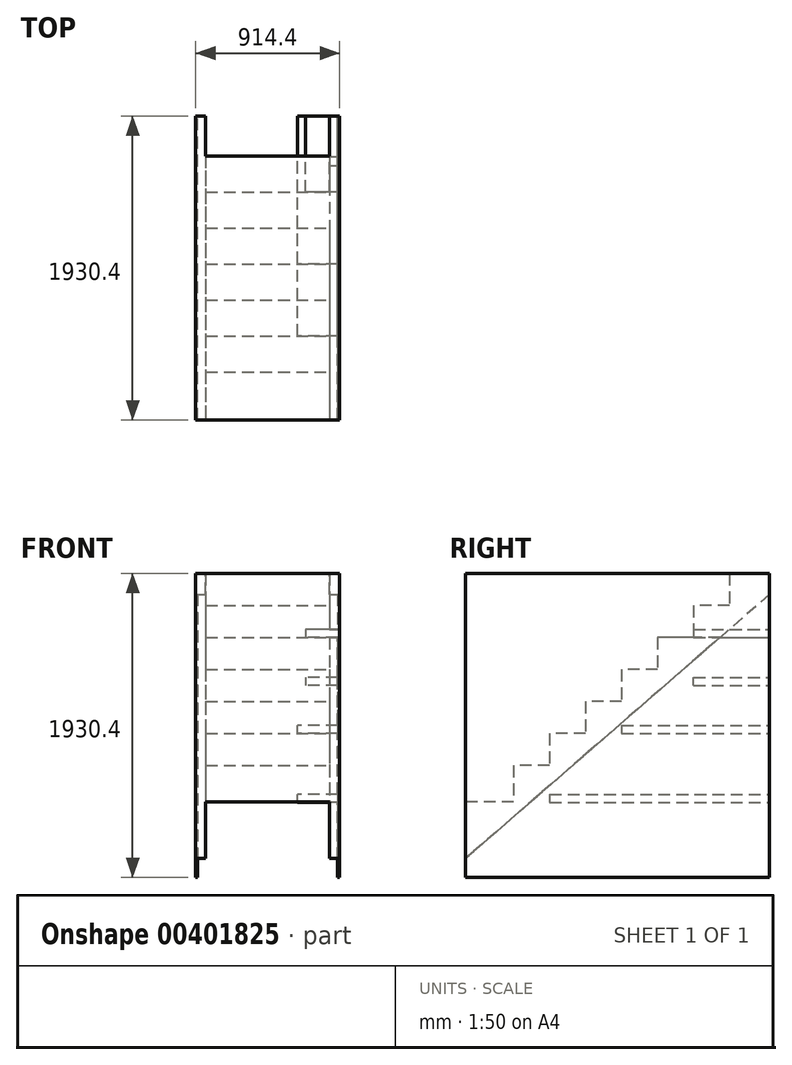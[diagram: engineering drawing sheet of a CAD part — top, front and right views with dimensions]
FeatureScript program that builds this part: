
annotation { "Feature Type Name" : "Feature", "Feature Type Description" : "" }
export const myFeature = defineFeature(function(context is Context, id is Id, definition is map)
    precondition{}
    {
        {
            var Q0;
            Q0=qCreatedBy(makeId("Front.planeOp"),FACE);
            var sketch = newSketch(context, id + "F0", { "sketchPlane" : qUnion([Q0])});
            skLineSegment(sketch, "E0.bottom", {"start": v(-457.2, 965.2) * mm, "end": v(457.2, 965.2) * mm});
            skLineSegment(sketch, "E0.top", {"start": v(-457.2, -965.2) * mm, "end": v(457.2, -965.2) * mm});
            skLineSegment(sketch, "E0.left", {"start": v(-457.2, 965.2) * mm, "end": v(-457.2, -965.2) * mm});
            skLineSegment(sketch, "E0.right", {"start": v(457.2, 965.2) * mm, "end": v(457.2, -965.2) * mm});
            skPoint(sketch, "E0.middle", {"position": v(0, 0) * mm});
            skSolve(sketch);
        }
        {
            var Q0;
            Q0 = qSketchRegion(id + "F0", true);
            extrude(context, id + "F1", {"entities" : qUnion([Q0]), "depth" : 1930.4 * mm});
        }
        {
            var Q0;
            Q0=qCreatedBy(makeId("Right.planeOp"),FACE);
            var sketch = newSketch(context, id + "F2", { "sketchPlane" : qUnion([Q0])});
            skLineSegment(sketch, "E1", {"start": v(-254, 965.2) * mm, "end": v(-254, 762) * mm});
            skLineSegment(sketch, "E2", {"start": v(-254, 762) * mm, "end": v(-482.6, 762) * mm});
            skLineSegment(sketch, "E3", {"start": v(-482.6, 762) * mm, "end": v(-482.6, 558.8) * mm});
            skLineSegment(sketch, "E4", {"start": v(-482.6, 558.8) * mm, "end": v(-711.2, 558.8) * mm});
            skLineSegment(sketch, "E5", {"start": v(-711.2, 558.8) * mm, "end": v(-711.2, 355.6) * mm});
            skLineSegment(sketch, "E6", {"start": v(-711.2, 355.6) * mm, "end": v(-939.8, 355.6) * mm});
            skLineSegment(sketch, "E7", {"start": v(-939.8, 355.6) * mm, "end": v(-939.8, 152.4) * mm});
            skLineSegment(sketch, "E8", {"start": v(-939.8, 152.4) * mm, "end": v(-1168.4, 152.4) * mm});
            skLineSegment(sketch, "E9", {"start": v(-1168.4, 152.4) * mm, "end": v(-1168.4, -50.8) * mm});
            skLineSegment(sketch, "E10", {"start": v(-1168.4, -50.8) * mm, "end": v(-1397, -50.8) * mm});
            skLineSegment(sketch, "E11", {"start": v(-1397, -50.8) * mm, "end": v(-1397, -254) * mm});
            skLineSegment(sketch, "E12", {"start": v(-1397, -254) * mm, "end": v(-1625.6, -254) * mm});
            skLineSegment(sketch, "E13", {"start": v(-1625.6, -254) * mm, "end": v(-1625.6, -485.14) * mm});
            skLineSegment(sketch, "E14", {"start": v(-1625.6, -485.14) * mm, "end": v(-1930.4, -485.14) * mm});
            skLineSegment(sketch, "E15", {"start": v(-1930.4, -485.14) * mm, "end": v(-1930.4, -969.01) * mm});
            skLineSegment(sketch, "E16", {"start": v(-1930.4, -969.01) * mm, "end": v(215.37, -969.01) * mm});
            skLineSegment(sketch, "E17", {"start": v(215.37, -969.01) * mm, "end": v(81.87, 972) * mm});
            skLineSegment(sketch, "E18", {"start": v(81.87, 972) * mm, "end": v(-254, 965.2) * mm});
            skSolve(sketch);
        }
        {
            var Q0;
            Q0 = qSketchRegion(id + "F2", true);
            extrude(context, id + "F3", {"entities" : qUnion([Q0]), "operationType" : NewBodyOperationType.REMOVE, "oppositeDirection" : true, "depth" : 393.7 * mm, "hasSecondDirection" : true, "secondDirectionOppositeDirection" : false, "secondDirectionDepth" : 393.7 * mm});
        }
        {
            var Q0;
            Q0=qCreatedBy(makeId("Right.planeOp"),FACE);
            var sketch = newSketch(context, id + "F4", { "sketchPlane" : qUnion([Q0])});
            skLineSegment(sketch, "E19", {"start": v(0, 832.77) * mm, "end": v(-1940.56, -853.72) * mm});
            skLineSegment(sketch, "E20", {"start": v(-1940.56, -853.72) * mm, "end": v(-2034.84, -1000.37) * mm});
            skLineSegment(sketch, "E21", {"start": v(-2034.84, -1000.37) * mm, "end": v(233.01, -1000.37) * mm});
            skLineSegment(sketch, "E22", {"start": v(233.01, -1000.37) * mm, "end": v(0, 832.77) * mm});
            skSolve(sketch);
        }
        {
            var Q0;
            Q0 = qSketchRegion(id + "F4", true);
            extrude(context, id + "F5", {"entities" : qUnion([Q0]), "operationType" : NewBodyOperationType.REMOVE, "oppositeDirection" : true, "depth" : 444.5 * mm, "hasSecondDirection" : true, "secondDirectionOppositeDirection" : false, "secondDirectionDepth" : 444.5 * mm});
        }
        {
            var Q0;
            {var subQ0=sQuery(id+"F0.wireOp",EDGE,"E0.bottom");var subQ1=sQuery(id+"F0.wireOp",EDGE,"E0.right");var subQ2=sQuery(id+"F0.wireOp",EDGE,"E0.top");Q0=makeQuery(id+"F3.boolean.opBoolean","SPLIT",FACE,{"disambiguationData":[TD([makeQuery(id+"F1.opExtrude","SWEPT_FACE",FACE,{"disambiguationData":[OSD([subQ1])]})])],"derivedFrom":makeQuery(id+"F1.opExtrude","CAP_FACE",FACE,{"disambiguationData":[OSD([subQ0,subQ2,sQuery(id+"F0.wireOp",EDGE,"E0.left"),subQ1])],"isStart":true})});}
            var sketch = newSketch(context, id + "F6", { "sketchPlane" : qUnion([Q0])});
            skLineSegment(sketch, "E23.bottom", {"start": v(-444.5, -488.95) * mm, "end": v(-190.5, -488.95) * mm});
            skLineSegment(sketch, "E23.top", {"start": v(-444.5, -438.15) * mm, "end": v(-190.5, -438.15) * mm});
            skLineSegment(sketch, "E23.left", {"start": v(-444.5, -488.95) * mm, "end": v(-444.5, -438.15) * mm});
            skLineSegment(sketch, "E23.right", {"start": v(-190.5, -488.95) * mm, "end": v(-190.5, -438.15) * mm});
            skLineSegment(sketch, "E24.bottom", {"start": v(-444.5, -50.8) * mm, "end": v(-190.5, -50.8) * mm});
            skLineSegment(sketch, "E24.top", {"start": v(-444.5, 0) * mm, "end": v(-190.5, 0) * mm});
            skLineSegment(sketch, "E24.left", {"start": v(-444.5, -50.8) * mm, "end": v(-444.5, 0) * mm});
            skLineSegment(sketch, "E24.right", {"start": v(-190.5, -50.8) * mm, "end": v(-190.5, 0) * mm});
            skLineSegment(sketch, "E25.bottom", {"start": v(-444.5, 304.8) * mm, "end": v(-241.3, 304.8) * mm});
            skLineSegment(sketch, "E25.top", {"start": v(-444.5, 254) * mm, "end": v(-241.3, 254) * mm});
            skLineSegment(sketch, "E25.left", {"start": v(-444.5, 304.8) * mm, "end": v(-444.5, 254) * mm});
            skLineSegment(sketch, "E25.right", {"start": v(-241.3, 304.8) * mm, "end": v(-241.3, 254) * mm});
            skLineSegment(sketch, "E26.bottom", {"start": v(-444.5, 609.6) * mm, "end": v(-241.3, 609.6) * mm});
            skLineSegment(sketch, "E26.top", {"start": v(-444.5, 558.8) * mm, "end": v(-241.3, 558.8) * mm});
            skLineSegment(sketch, "E26.left", {"start": v(-444.5, 609.6) * mm, "end": v(-444.5, 558.8) * mm});
            skLineSegment(sketch, "E26.right", {"start": v(-241.3, 609.6) * mm, "end": v(-241.3, 558.8) * mm});
            skSolve(sketch);
        }
        {
            var Q0;
            Q0 = qSketchRegion(id + "F6", true);
            var Q1;
            Q1=makeQuery(id+"F3.boolean.opBoolean","COPY",FACE,{"derivedFrom":makeQuery(id+"F3.opExtrude","SWEPT_FACE",FACE,{"disambiguationData":[OSD([sQuery(id+"F2.wireOp",EDGE,"E3")])]})});
            extrude(context, id + "F7", {"entities" : qUnion([Q0]), "operationType" : NewBodyOperationType.ADD, "endBound" : BoundingType.UP_TO_SURFACE, "oppositeDirection" : true, "endBoundEntityFace" : qUnion([Q1]), "depth" : 614.68 * mm});
        }
        {
            var Q0;
            {var subQ0=sQuery(id+"F0.wireOp",EDGE,"E0.bottom");var subQ1=sQuery(id+"F0.wireOp",EDGE,"E0.right");var subQ2=sQuery(id+"F0.wireOp",EDGE,"E0.top");Q0=makeQuery(id+"F7.boolean.opBoolean","MERGE",FACE,{"derivedFrom":[makeQuery(id+"F3.boolean.opBoolean","SPLIT",FACE,{"disambiguationData":[TD([makeQuery(id+"F1.opExtrude","SWEPT_FACE",FACE,{"disambiguationData":[OSD([subQ1])]})])],"derivedFrom":makeQuery(id+"F1.opExtrude","CAP_FACE",FACE,{"disambiguationData":[OSD([subQ0,subQ2,sQuery(id+"F0.wireOp",EDGE,"E0.left"),subQ1])],"isStart":true})}),makeQuery(id+"F7.opExtrude","CAP_FACE",FACE,{"disambiguationData":[OSD([sQuery(id+"F6.wireOp",EDGE,"E23.bottom"),sQuery(id+"F6.wireOp",EDGE,"E23.top"),sQuery(id+"F6.wireOp",EDGE,"E23.left"),sQuery(id+"F6.wireOp",EDGE,"E23.right")])],"isStart":true}),makeQuery(id+"F7.opExtrude","CAP_FACE",FACE,{"disambiguationData":[OSD([sQuery(id+"F6.wireOp",EDGE,"E24.bottom"),sQuery(id+"F6.wireOp",EDGE,"E24.top"),sQuery(id+"F6.wireOp",EDGE,"E24.left"),sQuery(id+"F6.wireOp",EDGE,"E24.right")])],"isStart":true}),makeQuery(id+"F7.opExtrude","CAP_FACE",FACE,{"disambiguationData":[OSD([sQuery(id+"F6.wireOp",EDGE,"E25.bottom"),sQuery(id+"F6.wireOp",EDGE,"E25.top"),sQuery(id+"F6.wireOp",EDGE,"E25.left"),sQuery(id+"F6.wireOp",EDGE,"E25.right")])],"isStart":true}),makeQuery(id+"F7.opExtrude","CAP_FACE",FACE,{"disambiguationData":[OSD([sQuery(id+"F6.wireOp",EDGE,"E26.bottom"),sQuery(id+"F6.wireOp",EDGE,"E26.top"),sQuery(id+"F6.wireOp",EDGE,"E26.left"),sQuery(id+"F6.wireOp",EDGE,"E26.right")])],"isStart":true})]});}
            var sketch = newSketch(context, id + "F8", { "sketchPlane" : qUnion([Q0])});
            skLineSegment(sketch, "E27.bottom", {"start": v(-190.5, -438.15) * mm, "end": v(-444.5, -438.15) * mm});
            skLineSegment(sketch, "E27.top", {"start": v(-190.5, -488.95) * mm, "end": v(-444.5, -488.95) * mm});
            skLineSegment(sketch, "E27.left", {"start": v(-190.5, -438.15) * mm, "end": v(-190.5, -488.95) * mm});
            skLineSegment(sketch, "E27.right", {"start": v(-444.5, -438.15) * mm, "end": v(-444.5, -488.95) * mm});
            skSolve(sketch);
        }
        {
            var Q0;
            Q0 = qSketchRegion(id + "F8", true);
            var Q1;
            Q1=makeQuery(id+"F3.boolean.opBoolean","COPY",FACE,{"derivedFrom":makeQuery(id+"F3.opExtrude","SWEPT_FACE",FACE,{"disambiguationData":[OSD([sQuery(id+"F2.wireOp",EDGE,"E11")])]})});
            extrude(context, id + "F9", {"entities" : qUnion([Q0]), "operationType" : NewBodyOperationType.ADD, "endBound" : BoundingType.UP_TO_SURFACE, "oppositeDirection" : true, "endBoundEntityFace" : qUnion([Q1]), "depth" : 2054.86 * mm});
        }
        {
            var Q0;
            {var subQ0=sQuery(id+"F0.wireOp",EDGE,"E0.bottom");var subQ1=sQuery(id+"F0.wireOp",EDGE,"E0.right");var subQ2=sQuery(id+"F0.wireOp",EDGE,"E0.top");Q0=makeQuery(id+"F7.boolean.opBoolean","MERGE",FACE,{"derivedFrom":[makeQuery(id+"F3.boolean.opBoolean","SPLIT",FACE,{"disambiguationData":[TD([makeQuery(id+"F1.opExtrude","SWEPT_FACE",FACE,{"disambiguationData":[OSD([subQ1])]})])],"derivedFrom":makeQuery(id+"F1.opExtrude","CAP_FACE",FACE,{"disambiguationData":[OSD([subQ0,subQ2,sQuery(id+"F0.wireOp",EDGE,"E0.left"),subQ1])],"isStart":true})}),makeQuery(id+"F7.opExtrude","CAP_FACE",FACE,{"disambiguationData":[OSD([sQuery(id+"F6.wireOp",EDGE,"E23.bottom"),sQuery(id+"F6.wireOp",EDGE,"E23.top"),sQuery(id+"F6.wireOp",EDGE,"E23.left"),sQuery(id+"F6.wireOp",EDGE,"E23.right")])],"isStart":true}),makeQuery(id+"F7.opExtrude","CAP_FACE",FACE,{"disambiguationData":[OSD([sQuery(id+"F6.wireOp",EDGE,"E24.bottom"),sQuery(id+"F6.wireOp",EDGE,"E24.top"),sQuery(id+"F6.wireOp",EDGE,"E24.left"),sQuery(id+"F6.wireOp",EDGE,"E24.right")])],"isStart":true}),makeQuery(id+"F7.opExtrude","CAP_FACE",FACE,{"disambiguationData":[OSD([sQuery(id+"F6.wireOp",EDGE,"E25.bottom"),sQuery(id+"F6.wireOp",EDGE,"E25.top"),sQuery(id+"F6.wireOp",EDGE,"E25.left"),sQuery(id+"F6.wireOp",EDGE,"E25.right")])],"isStart":true}),makeQuery(id+"F7.opExtrude","CAP_FACE",FACE,{"disambiguationData":[OSD([sQuery(id+"F6.wireOp",EDGE,"E26.bottom"),sQuery(id+"F6.wireOp",EDGE,"E26.top"),sQuery(id+"F6.wireOp",EDGE,"E26.left"),sQuery(id+"F6.wireOp",EDGE,"E26.right")])],"isStart":true})]});}
            var sketch = newSketch(context, id + "F10", { "sketchPlane" : qUnion([Q0])});
            skLineSegment(sketch, "E28.bottom", {"start": v(-190.5, 0) * mm, "end": v(-444.5, 0) * mm});
            skLineSegment(sketch, "E28.top", {"start": v(-190.5, -50.8) * mm, "end": v(-444.5, -50.8) * mm});
            skLineSegment(sketch, "E28.left", {"start": v(-190.5, 0) * mm, "end": v(-190.5, -50.8) * mm});
            skLineSegment(sketch, "E28.right", {"start": v(-444.5, 0) * mm, "end": v(-444.5, -50.8) * mm});
            skSolve(sketch);
        }
        {
            var Q0;
            Q0 = qSketchRegion(id + "F10", true);
            var Q1;
            Q1=makeQuery(id+"F3.boolean.opBoolean","COPY",FACE,{"derivedFrom":makeQuery(id+"F3.opExtrude","SWEPT_FACE",FACE,{"disambiguationData":[OSD([sQuery(id+"F2.wireOp",EDGE,"E7")])]})});
            extrude(context, id + "F11", {"entities" : qUnion([Q0]), "operationType" : NewBodyOperationType.ADD, "endBound" : BoundingType.UP_TO_SURFACE, "oppositeDirection" : true, "endBoundEntityFace" : qUnion([Q1]), "depth" : 1539.24 * mm});
        }
    });
